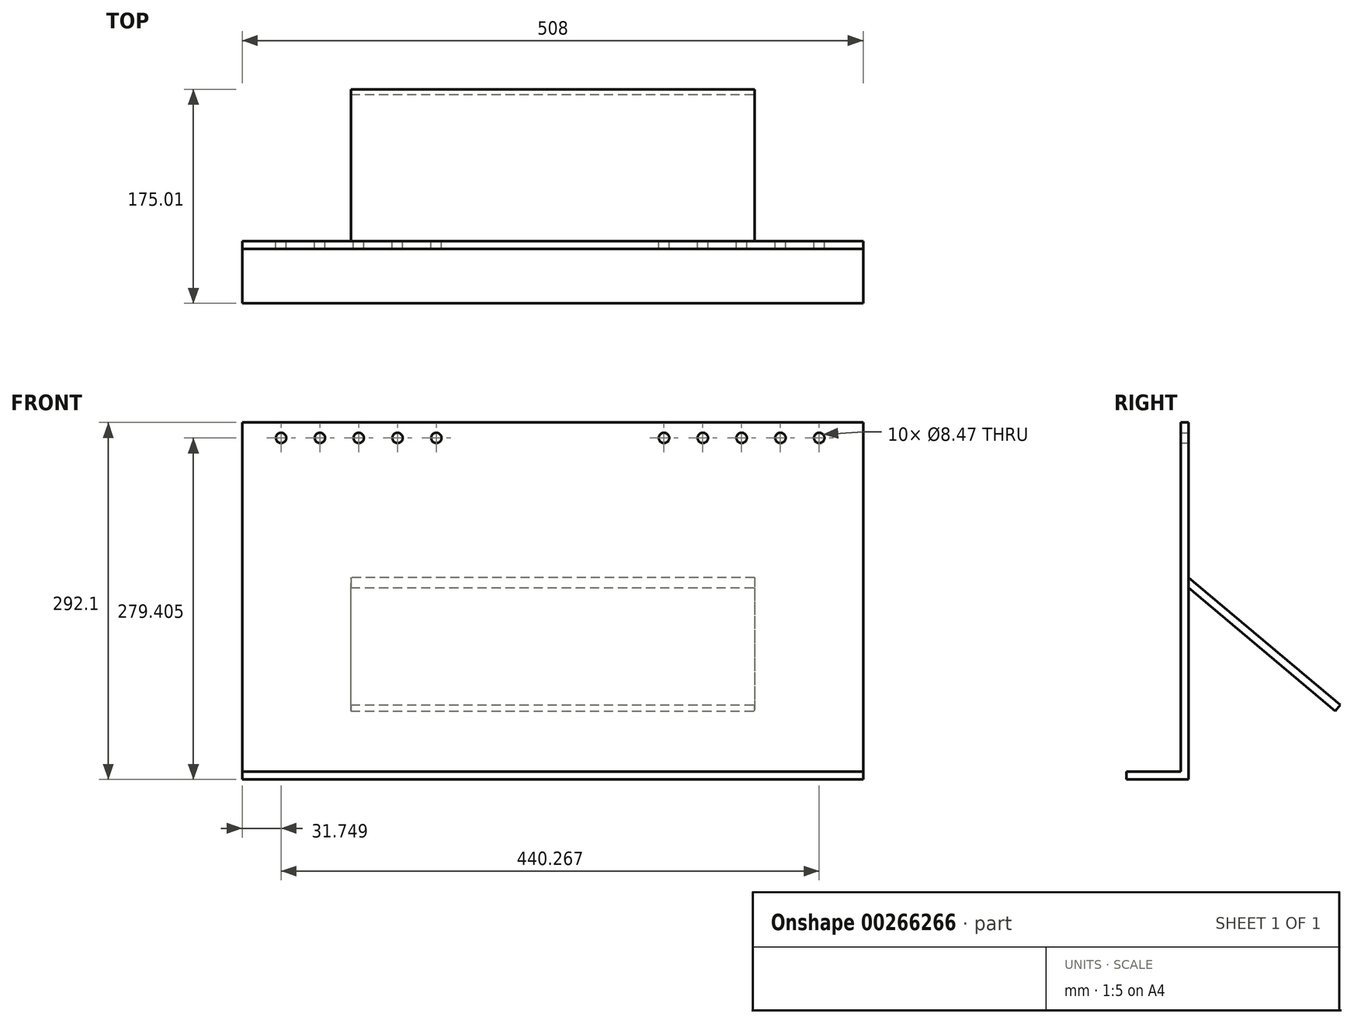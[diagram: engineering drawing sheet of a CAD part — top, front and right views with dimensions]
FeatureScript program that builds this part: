
annotation { "Feature Type Name" : "Feature", "Feature Type Description" : "" }
export const myFeature = defineFeature(function(context is Context, id is Id, definition is map)
    precondition{}
    {
        {
            var Q0;
            Q0=qCreatedBy(makeId("Front.planeOp"),FACE);
            var sketch = newSketch(context, id + "F0", { "sketchPlane" : qUnion([Q0])});
            skLineSegment(sketch, "E0.bottom", {"start": v(-254.77, 119.03) * mm, "end": v(253.23, 119.03) * mm});
            skLineSegment(sketch, "E0.top", {"start": v(-254.77, -166.72) * mm, "end": v(253.23, -166.72) * mm});
            skLineSegment(sketch, "E0.left", {"start": v(-254.77, 119.03) * mm, "end": v(-254.77, -173.07) * mm});
            skLineSegment(sketch, "E0.right", {"start": v(253.23, 119.03) * mm, "end": v(253.23, -173.07) * mm});
            skLineSegment(sketch, "E1", {"start": v(-254.77, -173.07) * mm, "end": v(253.23, -173.07) * mm});
            skLineSegment(sketch, "E2", {"start": v(-254.77, 106.33) * mm, "end": v(253.23, 106.33) * mm, "construction": true});
            skCircle(sketch, "E3", {"center": v(-223.02, 106.33) * mm, "radius": 4.23 * mm});
            skCircle(sketch, "E4", {"center": v(-191.27, 106.33) * mm, "radius": 4.23 * mm});
            skCircle(sketch, "E5", {"center": v(-159.52, 106.33) * mm, "radius": 4.23 * mm});
            skCircle(sketch, "E6", {"center": v(-127.77, 106.33) * mm, "radius": 4.23 * mm});
            skCircle(sketch, "E7", {"center": v(-96.02, 106.33) * mm, "radius": 4.23 * mm});
            skCircle(sketch, "E8", {"center": v(217.25, 106.33) * mm, "radius": 4.23 * mm});
            skCircle(sketch, "E9", {"center": v(185.5, 106.33) * mm, "radius": 4.23 * mm});
            skCircle(sketch, "E10", {"center": v(153.75, 106.33) * mm, "radius": 4.23 * mm});
            skCircle(sketch, "E11", {"center": v(122, 106.33) * mm, "radius": 4.23 * mm});
            skCircle(sketch, "E12", {"center": v(90.25, 106.33) * mm, "radius": 4.23 * mm});
            skSolve(sketch);
        }
        {
            var Q0;
            {var subQ0=sQuery(id+"F0.wireOp",EDGE,"E0.bottom");Q0=makeQuery(id+"F0.imprint","IMPRINT",FACE,{"disambiguationData":[TD([[makeQuery(id+"F0.imprint","IMPRINT",EDGE,{"derivedFrom":subQ0}),-1.0]])]});}
            extrude(context, id + "F1", {"entities" : qUnion([Q0]), "depth" : 6.35 * mm});
        }
        {
            var Q0;
            {var subQ0=sQuery(id+"F0.wireOp",EDGE,"E0.top");Q0=makeQuery(id+"F0.imprint","IMPRINT",FACE,{"disambiguationData":[TD([[makeQuery(id+"F0.imprint","IMPRINT",EDGE,{"derivedFrom":subQ0}),-1.0]])]});}
            extrude(context, id + "F2", {"entities" : qUnion([Q0]), "operationType" : NewBodyOperationType.ADD, "depth" : 50.8 * mm});
        }
        {
            var Q0;
            {var subQ0=sQuery(id+"F0.wireOp",EDGE,"E0.bottom");Q0=makeQuery(id+"F0.imprint","IMPRINT",FACE,{"disambiguationData":[TD([[makeQuery(id+"F0.imprint","IMPRINT",EDGE,{"derivedFrom":subQ0}),-1.0]])]});}
            var sketch = newSketch(context, id + "F3", { "sketchPlane" : qUnion([Q0])});
            skLineSegment(sketch, "E13.bottom", {"start": v(164.33, -7.97) * mm, "end": v(-165.87, -7.97) * mm});
            skLineSegment(sketch, "E13.left", {"start": v(164.33, -7.97) * mm, "end": v(164.33, -173.07) * mm});
            skLineSegment(sketch, "E13.right", {"start": v(-165.87, -7.97) * mm, "end": v(-165.87, -173.07) * mm});
            skLineSegment(sketch, "E14.0", {"start": v(-254.77, -173.07) * mm, "end": v(253.23, -173.07) * mm});
            skSolve(sketch);
        }
        {
            var Q0;
            Q0 = qSketchRegion(id + "F3", true);
            extrude(context, id + "F4", {"entities" : qUnion([Q0]), "operationType" : NewBodyOperationType.ADD, "oppositeDirection" : true, "depth" : 152.4 * mm});
        }
        {
            var Q0;
            Q0=makeQuery(id+"F4.opExtrude","SWEPT_FACE",FACE,{"disambiguationData":[OSD([sQuery(id+"F3.wireOp",EDGE,"E13.left")])]});
            var sketch = newSketch(context, id + "F5", { "sketchPlane" : qUnion([Q0])});
            skLineSegment(sketch, "E15", {"start": v(0, -16.25) * mm, "end": v(120.12, -117.05) * mm});
            skLineSegment(sketch, "E16", {"start": v(120.12, -117.05) * mm, "end": v(0, -173.07) * mm});
            skLineSegment(sketch, "E17", {"start": v(0, -16.25) * mm, "end": v(0, -173.07) * mm});
            skLineSegment(sketch, "E18", {"start": v(0, -7.97) * mm, "end": v(124.2, -112.19) * mm});
            skLineSegment(sketch, "E19", {"start": v(120.12, -117.05) * mm, "end": v(124.2, -112.19) * mm});
            skSolve(sketch);
        }
        {
            var Q0;
            Q0=makeQuery(id+"F5.imprint","IMPRINT",FACE,{"disambiguationData":[TD([[makeQuery(id+"F5.imprint","IMPRINT",EDGE,{"derivedFrom":sQuery(id+"F5.wireOp",EDGE,"E16")}),1.0]])]});
            var Q1;
            Q1=makeQuery(id+"F5.imprint","IMPRINT",FACE,{"disambiguationData":[TD([[makeQuery(id+"F5.imprint","IMPRINT",EDGE,{"derivedFrom":sQuery(id+"F5.wireOp",EDGE,"E15")}),-1.0]])]});
            extrude(context, id + "F6", {"entities" : qUnion([Q0, Q1]), "operationType" : NewBodyOperationType.REMOVE, "endBound" : BoundingType.THROUGH_ALL, "oppositeDirection" : true, "depth" : 25.4 * mm});
        }
    });
